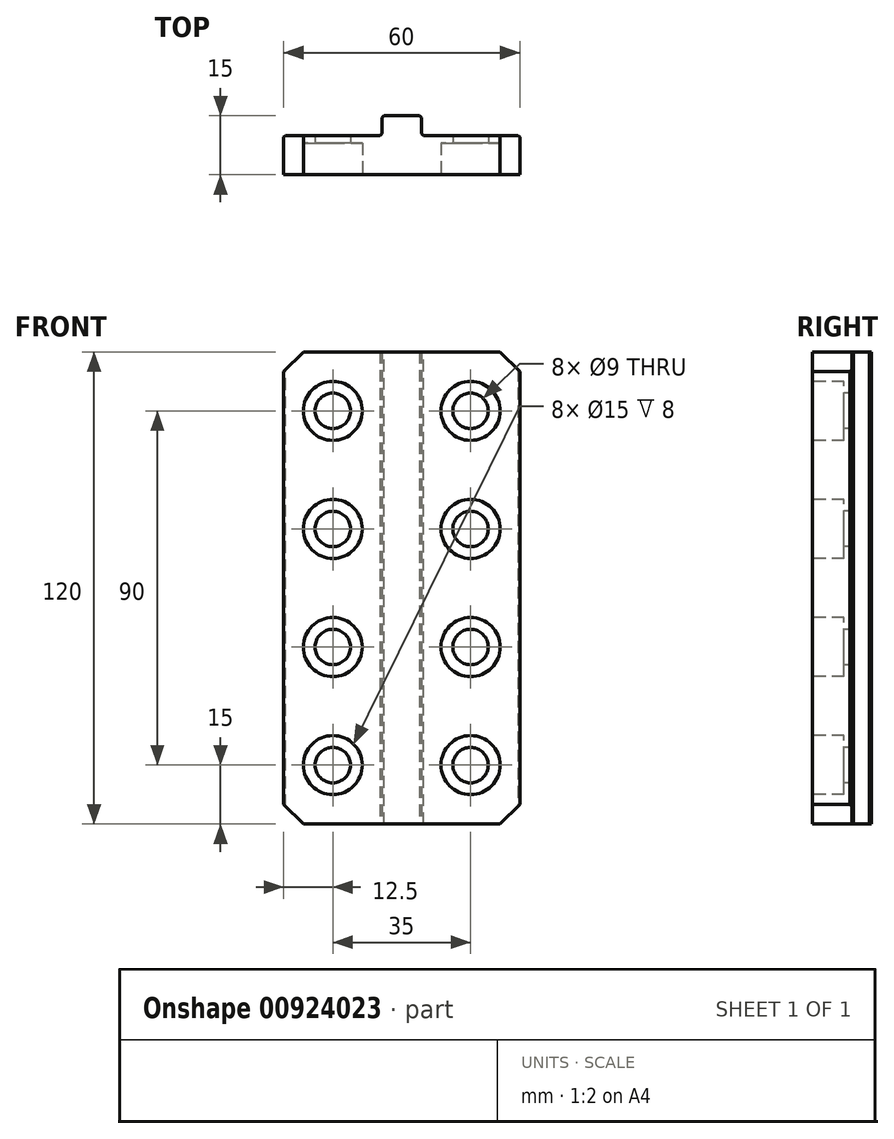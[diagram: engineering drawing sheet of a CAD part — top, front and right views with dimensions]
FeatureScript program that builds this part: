
annotation { "Feature Type Name" : "Feature", "Feature Type Description" : "" }
export const myFeature = defineFeature(function(context is Context, id is Id, definition is map)
    precondition{}
    {
        {
            var Q0;
            Q0=qCreatedBy(makeId("Top.planeOp"),FACE);
            var sketch = newSketch(context, id + "F0", { "sketchPlane" : qUnion([Q0])});
            skLineSegment(sketch, "E0", {"start": v(0, 0) * mm, "end": v(60, 0) * mm});
            skLineSegment(sketch, "E1", {"start": v(60, 0) * mm, "end": v(60, 10) * mm});
            skLineSegment(sketch, "E2", {"start": v(60, 10) * mm, "end": v(35, 10) * mm});
            skLineSegment(sketch, "E3", {"start": v(35, 10) * mm, "end": v(35, 15) * mm});
            skLineSegment(sketch, "E4", {"start": v(35, 15) * mm, "end": v(25, 15) * mm});
            skLineSegment(sketch, "E5", {"start": v(25, 15) * mm, "end": v(25, 10) * mm});
            skLineSegment(sketch, "E6", {"start": v(25, 10) * mm, "end": v(0, 10) * mm});
            skLineSegment(sketch, "E7", {"start": v(0, 10) * mm, "end": v(0, 0) * mm});
            skSolve(sketch);
        }
        {
            var Q0;
            Q0=makeQuery(id+"F0.imprint","IMPRINT",FACE,{"disambiguationData":[TD([[makeQuery(id+"F0.imprint","IMPRINT",EDGE,{"derivedFrom":sQuery(id+"F0.wireOp",EDGE,"E0")}),1.0]])]});
            extrude(context, id + "F1", {"entities" : qUnion([Q0]), "depth" : 120 * mm, "offsetDistance" : 25 * mm});
        }
        {
            var Q0;
            Q0=makeQuery(id+"F1.opExtrude","SWEPT_FACE",FACE,{"disambiguationData":[OSD([sQuery(id+"F0.wireOp",EDGE,"E0")])]});
            var sketch = newSketch(context, id + "F2", { "sketchPlane" : qUnion([Q0])});
            skPoint(sketch, "E8", {"position": v(12.5, 105) * mm});
            skPoint(sketch, "E9", {"position": v(12.5, 75) * mm});
            skPoint(sketch, "E10", {"position": v(12.5, 45) * mm});
            skPoint(sketch, "E11", {"position": v(12.5, 15) * mm});
            skPoint(sketch, "E12", {"position": v(47.5, 105) * mm});
            skPoint(sketch, "E13", {"position": v(47.5, 75) * mm});
            skPoint(sketch, "E14", {"position": v(47.5, 45) * mm});
            skPoint(sketch, "E15", {"position": v(47.5, 15) * mm});
            skSolve(sketch);
        }
        {
            var Q0;
            Q0=sQuery(id+"F2.wireOp",VERTEX,"E14");
            var Q1;
            Q1=sQuery(id+"F2.wireOp",VERTEX,"E13");
            var Q2;
            Q2=sQuery(id+"F2.wireOp",VERTEX,"E11");
            var Q3;
            Q3=sQuery(id+"F2.wireOp",VERTEX,"E8");
            var Q4;
            Q4=sQuery(id+"F2.wireOp",VERTEX,"E15");
            var Q5;
            Q5=sQuery(id+"F2.wireOp",VERTEX,"E9");
            var Q6;
            Q6=sQuery(id+"F2.wireOp",VERTEX,"E12");
            var Q7;
            Q7=sQuery(id+"F2.wireOp",VERTEX,"E10");
            var Q8;
            Q8=makeQuery(id+"F1.opExtrude","SWEPT_BODY",BODY,{"disambiguationData":[OSD([sQuery(id+"F0.wireOp",EDGE,"E0"),sQuery(id+"F0.wireOp",EDGE,"E1"),sQuery(id+"F0.wireOp",EDGE,"E2"),sQuery(id+"F0.wireOp",EDGE,"E3"),sQuery(id+"F0.wireOp",EDGE,"E4"),sQuery(id+"F0.wireOp",EDGE,"E5"),sQuery(id+"F0.wireOp",EDGE,"E6"),sQuery(id+"F0.wireOp",EDGE,"E7")])]});
            hole(context, id + "F3", {"style" : HoleStyle.C_BORE, "endStyle" : HoleEndStyle.BLIND, "standardTappedOrClearance" : lookupTablePath({ "standard" : "ISO", "size" : "9", "type" : "Drilled" }), "standardBlindInLast" : lookupTablePath({ "standard" : "ISO", "size" : "9", "type" : "Drilled" }), "holeDiameter" : 9 * mm, "cBoreDiameter" : 15 * mm, "cBoreDepth" : 8 * mm, "majorDiameter" : 5 * mm, "holeDepth" : 10 * mm, "isTappedThrough" : true, "tappedDepth" : 9 * mm, "tapClearance" : 3, "startFromSketch" : true, "locations" : qUnion([Q0, Q1, Q2, Q3, Q4, Q5, Q6, Q7]), "scope" : qUnion([Q8])});
        }
        {
            var Q0;
            Q0=makeQuery(id+"F1.opExtrude","CAP_EDGE",EDGE,{"disambiguationData":[OSD([sQuery(id+"F0.wireOp",EDGE,"E7")])],"isStart":false});
            var Q1;
            {var subQ0=sQuery(id+"F0.wireOp",EDGE,"E7");var subQ1=sQuery(id+"F0.wireOp",EDGE,"E6");Q1=makeQuery(id+"F5.opChamfer","BLEND_EDGE",EDGE,{"blendedFrom":[makeQuery(id+"F1.opExtrude","SWEPT_EDGE",EDGE,{"disambiguationData":[OSD([subQ1,subQ0])]}),makeQuery(id+"F1.opExtrude","CAP_FACE",FACE,{"disambiguationData":[OSD([sQuery(id+"F0.wireOp",EDGE,"E0"),sQuery(id+"F0.wireOp",EDGE,"E1"),sQuery(id+"F0.wireOp",EDGE,"E2"),sQuery(id+"F0.wireOp",EDGE,"E3"),sQuery(id+"F0.wireOp",EDGE,"E4"),sQuery(id+"F0.wireOp",EDGE,"E5"),subQ1,subQ0])],"isStart":false})],"blendedInto":[makeQuery(id+"F1.opExtrude","CAP_FACE",FACE,{"disambiguationData":[OSD([sQuery(id+"F0.wireOp",EDGE,"E0"),sQuery(id+"F0.wireOp",EDGE,"E1"),sQuery(id+"F0.wireOp",EDGE,"E2"),sQuery(id+"F0.wireOp",EDGE,"E3"),sQuery(id+"F0.wireOp",EDGE,"E4"),sQuery(id+"F0.wireOp",EDGE,"E5"),subQ1,subQ0])],"isStart":false})]});}
            var Q2;
            Q2=makeQuery(id+"F1.opExtrude","CAP_EDGE",EDGE,{"disambiguationData":[OSD([sQuery(id+"F0.wireOp",EDGE,"E1")])],"isStart":false});
            var Q3;
            {var subQ0=sQuery(id+"F0.wireOp",EDGE,"E2");var subQ1=sQuery(id+"F0.wireOp",EDGE,"E1");Q3=makeQuery(id+"F5.opChamfer","BLEND_EDGE",EDGE,{"blendedFrom":[makeQuery(id+"F1.opExtrude","SWEPT_EDGE",EDGE,{"disambiguationData":[OSD([subQ1,subQ0])]}),makeQuery(id+"F1.opExtrude","CAP_FACE",FACE,{"disambiguationData":[OSD([sQuery(id+"F0.wireOp",EDGE,"E0"),subQ1,subQ0,sQuery(id+"F0.wireOp",EDGE,"E3"),sQuery(id+"F0.wireOp",EDGE,"E4"),sQuery(id+"F0.wireOp",EDGE,"E5"),sQuery(id+"F0.wireOp",EDGE,"E6"),sQuery(id+"F0.wireOp",EDGE,"E7")])],"isStart":false})],"blendedInto":[makeQuery(id+"F1.opExtrude","CAP_FACE",FACE,{"disambiguationData":[OSD([sQuery(id+"F0.wireOp",EDGE,"E0"),subQ1,subQ0,sQuery(id+"F0.wireOp",EDGE,"E3"),sQuery(id+"F0.wireOp",EDGE,"E4"),sQuery(id+"F0.wireOp",EDGE,"E5"),sQuery(id+"F0.wireOp",EDGE,"E6"),sQuery(id+"F0.wireOp",EDGE,"E7")])],"isStart":false})]});}
            var Q4;
            Q4=makeQuery(id+"F1.opExtrude","CAP_EDGE",EDGE,{"disambiguationData":[OSD([sQuery(id+"F0.wireOp",EDGE,"E1")])],"isStart":true});
            var Q5;
            {var subQ0=sQuery(id+"F0.wireOp",EDGE,"E2");var subQ1=sQuery(id+"F0.wireOp",EDGE,"E1");Q5=makeQuery(id+"F5.opChamfer","BLEND_EDGE",EDGE,{"blendedFrom":[makeQuery(id+"F1.opExtrude","SWEPT_EDGE",EDGE,{"disambiguationData":[OSD([subQ1,subQ0])]}),makeQuery(id+"F1.opExtrude","CAP_FACE",FACE,{"disambiguationData":[OSD([sQuery(id+"F0.wireOp",EDGE,"E0"),subQ1,subQ0,sQuery(id+"F0.wireOp",EDGE,"E3"),sQuery(id+"F0.wireOp",EDGE,"E4"),sQuery(id+"F0.wireOp",EDGE,"E5"),sQuery(id+"F0.wireOp",EDGE,"E6"),sQuery(id+"F0.wireOp",EDGE,"E7")])],"isStart":true})],"blendedInto":[makeQuery(id+"F1.opExtrude","CAP_FACE",FACE,{"disambiguationData":[OSD([sQuery(id+"F0.wireOp",EDGE,"E0"),subQ1,subQ0,sQuery(id+"F0.wireOp",EDGE,"E3"),sQuery(id+"F0.wireOp",EDGE,"E4"),sQuery(id+"F0.wireOp",EDGE,"E5"),sQuery(id+"F0.wireOp",EDGE,"E6"),sQuery(id+"F0.wireOp",EDGE,"E7")])],"isStart":true})]});}
            var Q6;
            Q6=makeQuery(id+"F1.opExtrude","CAP_EDGE",EDGE,{"disambiguationData":[OSD([sQuery(id+"F0.wireOp",EDGE,"E7")])],"isStart":true});
            var Q7;
            {var subQ0=sQuery(id+"F0.wireOp",EDGE,"E7");var subQ1=sQuery(id+"F0.wireOp",EDGE,"E6");Q7=makeQuery(id+"F5.opChamfer","BLEND_EDGE",EDGE,{"blendedFrom":[makeQuery(id+"F1.opExtrude","SWEPT_EDGE",EDGE,{"disambiguationData":[OSD([subQ1,subQ0])]}),makeQuery(id+"F1.opExtrude","CAP_FACE",FACE,{"disambiguationData":[OSD([sQuery(id+"F0.wireOp",EDGE,"E0"),sQuery(id+"F0.wireOp",EDGE,"E1"),sQuery(id+"F0.wireOp",EDGE,"E2"),sQuery(id+"F0.wireOp",EDGE,"E3"),sQuery(id+"F0.wireOp",EDGE,"E4"),sQuery(id+"F0.wireOp",EDGE,"E5"),subQ1,subQ0])],"isStart":true})],"blendedInto":[makeQuery(id+"F1.opExtrude","CAP_FACE",FACE,{"disambiguationData":[OSD([sQuery(id+"F0.wireOp",EDGE,"E0"),sQuery(id+"F0.wireOp",EDGE,"E1"),sQuery(id+"F0.wireOp",EDGE,"E2"),sQuery(id+"F0.wireOp",EDGE,"E3"),sQuery(id+"F0.wireOp",EDGE,"E4"),sQuery(id+"F0.wireOp",EDGE,"E5"),subQ1,subQ0])],"isStart":true})]});}
            chamfer(context, id + "F4", {"entities" : qUnion([Q0, Q1, Q2, Q3, Q4, Q5, Q6, Q7]), "width" : 5 * mm, "tangentPropagation" : true});
        }
        {
            var Q0;
            Q0=makeQuery(id+"F1.opExtrude","SWEPT_EDGE",EDGE,{"disambiguationData":[OSD([sQuery(id+"F0.wireOp",EDGE,"E3"),sQuery(id+"F0.wireOp",EDGE,"E4")])]});
            var Q1;
            Q1=makeQuery(id+"F1.opExtrude","SWEPT_EDGE",EDGE,{"disambiguationData":[OSD([sQuery(id+"F0.wireOp",EDGE,"E4"),sQuery(id+"F0.wireOp",EDGE,"E5")])]});
            var Q2;
            Q2=makeQuery(id+"F1.opExtrude","SWEPT_EDGE",EDGE,{"disambiguationData":[OSD([sQuery(id+"F0.wireOp",EDGE,"E6"),sQuery(id+"F0.wireOp",EDGE,"E7")])]});
            var Q3;
            Q3=makeQuery(id+"F1.opExtrude","SWEPT_EDGE",EDGE,{"disambiguationData":[OSD([sQuery(id+"F0.wireOp",EDGE,"E1"),sQuery(id+"F0.wireOp",EDGE,"E2")])]});
            var Q4;
            Q4=makeQuery(id+"F1.opExtrude","SWEPT_EDGE",EDGE,{"disambiguationData":[OSD([sQuery(id+"F0.wireOp",EDGE,"E2"),sQuery(id+"F0.wireOp",EDGE,"E3")])]});
            var Q5;
            Q5=makeQuery(id+"F1.opExtrude","SWEPT_EDGE",EDGE,{"disambiguationData":[OSD([sQuery(id+"F0.wireOp",EDGE,"E5"),sQuery(id+"F0.wireOp",EDGE,"E6")])]});
            chamfer(context, id + "F5", {"entities" : qUnion([Q0, Q1, Q2, Q3, Q4, Q5]), "width" : 0.5 * mm, "tangentPropagation" : true});
        }
    });
